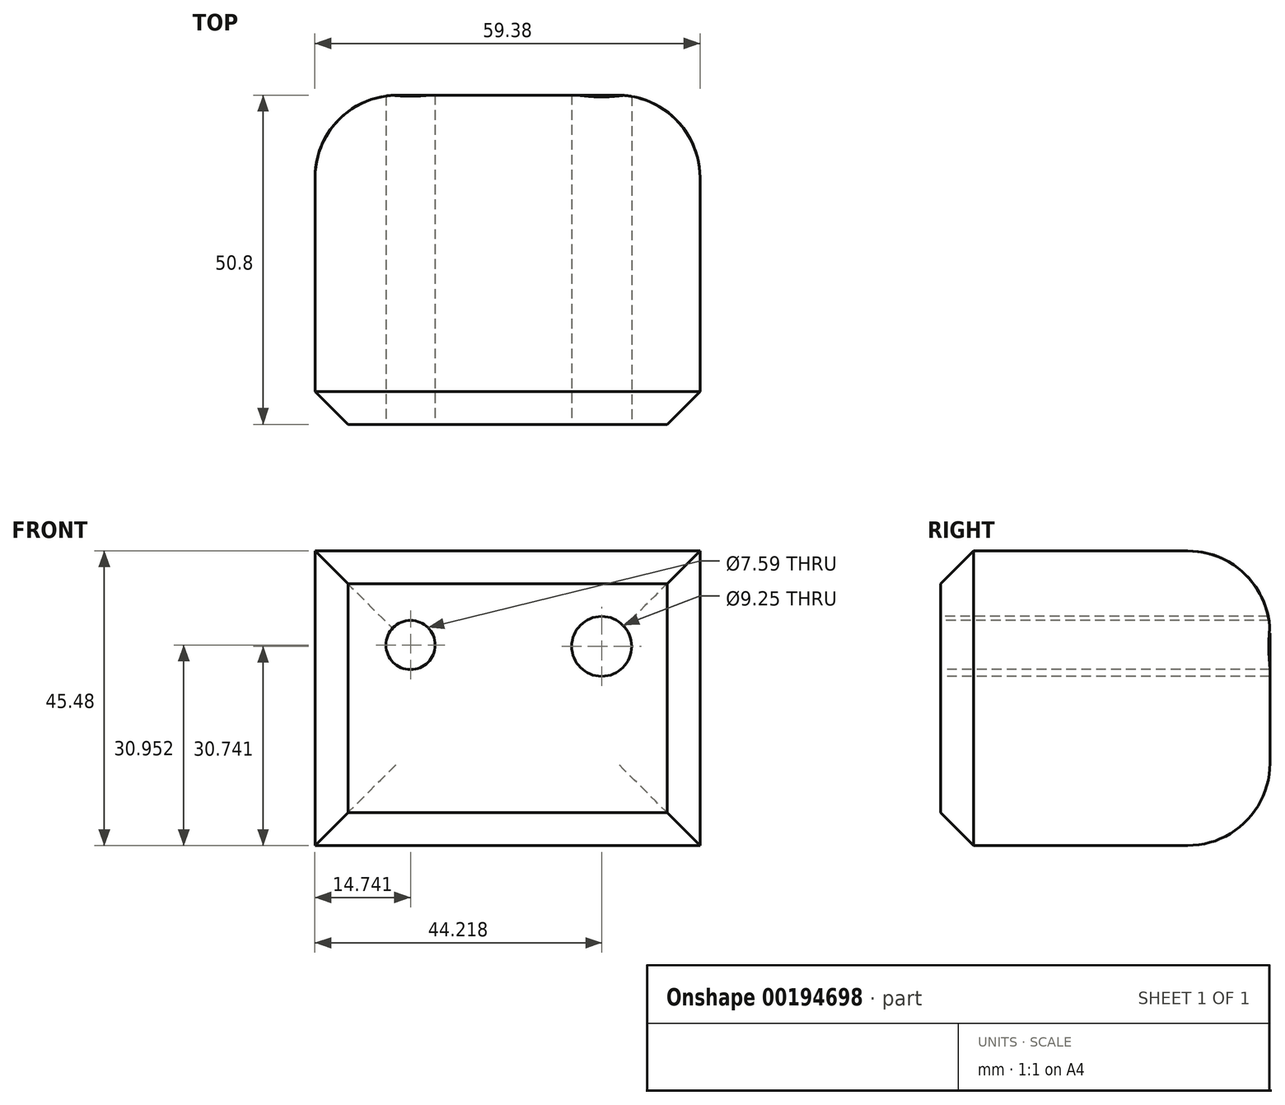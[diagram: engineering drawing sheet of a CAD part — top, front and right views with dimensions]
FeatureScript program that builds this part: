
annotation { "Feature Type Name" : "Feature", "Feature Type Description" : "" }
export const myFeature = defineFeature(function(context is Context, id is Id, definition is map)
    precondition{}
    {
        {
            var Q0;
            Q0=qCreatedBy(makeId("Front.planeOp"),FACE);
            var sketch = newSketch(context, id + "F0", { "sketchPlane" : qUnion([Q0])});
            skLineSegment(sketch, "E0.bottom", {"start": v(29.69, 22.74) * mm, "end": v(-29.69, 22.74) * mm});
            skLineSegment(sketch, "E0.top", {"start": v(29.69, -22.74) * mm, "end": v(-29.69, -22.74) * mm});
            skLineSegment(sketch, "E0.left", {"start": v(29.69, 22.74) * mm, "end": v(29.69, -22.74) * mm});
            skLineSegment(sketch, "E0.right", {"start": v(-29.69, 22.74) * mm, "end": v(-29.69, -22.74) * mm});
            skPoint(sketch, "E0.middle", {"position": v(0, 0) * mm});
            skSolve(sketch);
        }
        {
            var Q0;
            Q0=makeQuery(id+"F0.imprint","IMPRINT",FACE,{"disambiguationData":[TD([[makeQuery(id+"F0.imprint","IMPRINT",EDGE,{"derivedFrom":sQuery(id+"F0.wireOp",EDGE,"E0.bottom")}),1.0]])]});
            extrude(context, id + "F1", {"entities" : qUnion([Q0]), "depth" : 50.8 * mm});
        }
        {
            var Q0;
            Q0=makeQuery(id+"F1.opExtrude","CAP_EDGE",EDGE,{"disambiguationData":[OSD([sQuery(id+"F0.wireOp",EDGE,"E0.bottom")])],"isStart":false});
            var Q1;
            Q1=makeQuery(id+"F1.opExtrude","CAP_EDGE",EDGE,{"disambiguationData":[OSD([sQuery(id+"F0.wireOp",EDGE,"E0.left")])],"isStart":false});
            var Q2;
            Q2=makeQuery(id+"F1.opExtrude","CAP_EDGE",EDGE,{"disambiguationData":[OSD([sQuery(id+"F0.wireOp",EDGE,"E0.top")])],"isStart":false});
            var Q3;
            Q3=makeQuery(id+"F1.opExtrude","CAP_EDGE",EDGE,{"disambiguationData":[OSD([sQuery(id+"F0.wireOp",EDGE,"E0.right")])],"isStart":false});
            chamfer(context, id + "F2", {"entities" : qUnion([Q0, Q1, Q2, Q3]), "width" : 5.08 * mm, "tangentPropagation" : true});
        }
        {
            var Q0;
            Q0=makeQuery(id+"F1.opExtrude","CAP_FACE",FACE,{"disambiguationData":[OSD([sQuery(id+"F0.wireOp",EDGE,"E0.bottom"),sQuery(id+"F0.wireOp",EDGE,"E0.top"),sQuery(id+"F0.wireOp",EDGE,"E0.left"),sQuery(id+"F0.wireOp",EDGE,"E0.right")])],"isStart":true});
            fillet(context, id + "F3", {"entities" : qUnion([Q0]), "radius" : 12.7 * mm, "tangentPropagation" : true, "allowEdgeOverflow" : false});
        }
        {
            var Q0;
            Q0=makeQuery(id+"F1.opExtrude","CAP_FACE",FACE,{"disambiguationData":[OSD([sQuery(id+"F0.wireOp",EDGE,"E0.bottom"),sQuery(id+"F0.wireOp",EDGE,"E0.top"),sQuery(id+"F0.wireOp",EDGE,"E0.left"),sQuery(id+"F0.wireOp",EDGE,"E0.right")])],"isStart":false});
            var sketch = newSketch(context, id + "F4", { "sketchPlane" : qUnion([Q0])});
            skCircle(sketch, "E1", {"center": v(-14.95, 8.21) * mm, "radius": 3.8 * mm});
            skCircle(sketch, "E2", {"center": v(14.53, 8) * mm, "radius": 4.62 * mm});
            skSolve(sketch);
        }
        {
            var Q0;
            Q0=makeQuery(id+"F4.imprint","IMPRINT",FACE,{"disambiguationData":[TD([[makeQuery(id+"F4.imprint","IMPRINT",EDGE,{"derivedFrom":sQuery(id+"F4.wireOp",EDGE,"E1")}),1.0]])]});
            var Q1;
            Q1=makeQuery(id+"F4.imprint","IMPRINT",FACE,{"disambiguationData":[TD([[makeQuery(id+"F4.imprint","IMPRINT",EDGE,{"derivedFrom":sQuery(id+"F4.wireOp",EDGE,"E2")}),1.0]])]});
            extrude(context, id + "F5", {"entities" : qUnion([Q0, Q1]), "operationType" : NewBodyOperationType.REMOVE, "oppositeDirection" : true, "depth" : 50.8 * mm});
        }
    });
